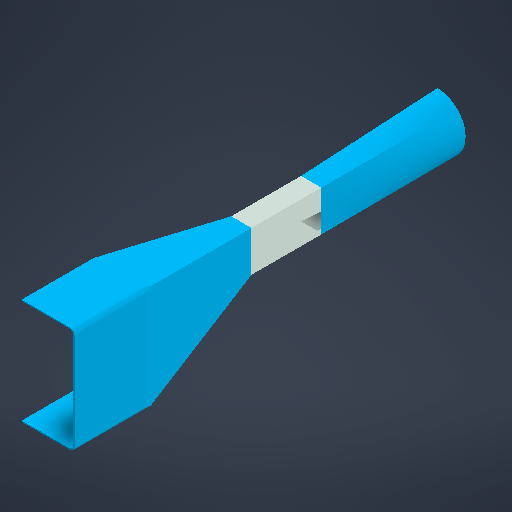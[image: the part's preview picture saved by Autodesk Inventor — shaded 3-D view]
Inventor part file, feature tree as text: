
AUTODESK INVENTOR PART (.ipt)
format: ipt  version: 2025 (Build 290162010, 162A)  size: 448,512 bytes
history: native  units: mm
features: sketch x8, plane x4, loft x4, other x4, extrude x3, fillet x3
ambient origin geometry x8: Origin, YZ Plane, XZ Plane, XY Plane, X Axis, Y Axis, Z Axis, Center Point
bodies: Solid1 (feature_tree)
feature tree (26):
  extrude  "Extrusion1"  Depth=180.0mm
  plane  "Work Plane1"
  sketch  "Sketch2"  dims[d2=5.0mm d3=310.0mm d4=0.0mm]
  plane  "Work Plane2"
  sketch  "Sketch3"  dims[d11=605.0mm d12=250.0mm]
  sketch  "Sketch4"  dims[d14=-90.0mm d15=605.0mm]
  loft  "Loft1"
  loft  "Loft2"
  plane  "Work Plane4"
  sketch  "Sketch5"  dims[d16=0.0mm d17=90.0deg d18=0.0mm d19=90.0deg]
  sketch  "Sketch6"  dims[d20=5.0mm d21=0.0mm d22=90.0deg d23=0.0mm d24=90.0deg d27=470.0mm d28=470.0mm]
  sketch  "Sketch7"  dims[d29=5.0mm d30=0.0mm d31=90.0deg]
  loft  "Loft3"
  loft  "Loft4"
  extrude  "Extrusion2"  TaperAngle=0.0deg  [1 undecoded]
  fillet  "Fillet1"  [1 undecoded]
  fillet  "Fillet2"  Radius=470.0mm
  fillet  "Fillet3"  Radius=470.0mm
  plane  "Work Plane5"
  extrude  "Extrusion3"  TaperAngle=0.0deg  [1 undecoded]
  sketch  "Sketch1"  dims[d0=180.0mm d1=180.0mm]
  other  "Edges1"
  other  "Edges2"
  other  "Edges3"
  other  "Edges4"
  sketch  "Sketch8"  dims[d32=0.0mm d33=90.0deg d34=0.0mm d35=90.0deg d36=0.0mm d37=90.0deg d38=320.0mm d39=0.0mm d40=20.0mm d41=20.0mm d42=20.0mm d43=320.0mm d44=0.0mm]
note: 3 required parameter values undecoded (feature->parameter linkage not recoverable at this tier; creation-order binding heuristic only, values carry confidence <= 0.55)
